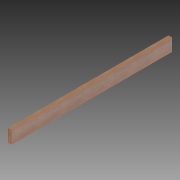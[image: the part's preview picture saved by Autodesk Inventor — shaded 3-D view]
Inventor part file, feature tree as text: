
AUTODESK INVENTOR PART (.ipt)
format: ipt  version: 2015 (Build 190159000, 159)  size: 77,312 bytes
history: native  units: in
note: dims shown in document units (in); Inventor stores cm internally (conversion verified against a paired STEP export)
features: extrude x1, sketch x1
ambient origin geometry x8: Origin, YZ Plane, XZ Plane, XY Plane, X Axis, Y Axis, Z Axis, Center Point
bodies: Solid1 (feature_tree)
feature tree (2):
  extrude  "Extrusion1"  Depth=5.5in
  sketch  "Sketch1"  dims[d0=1.5in d1=5.5in d2=69.48in d3=0.0in]
